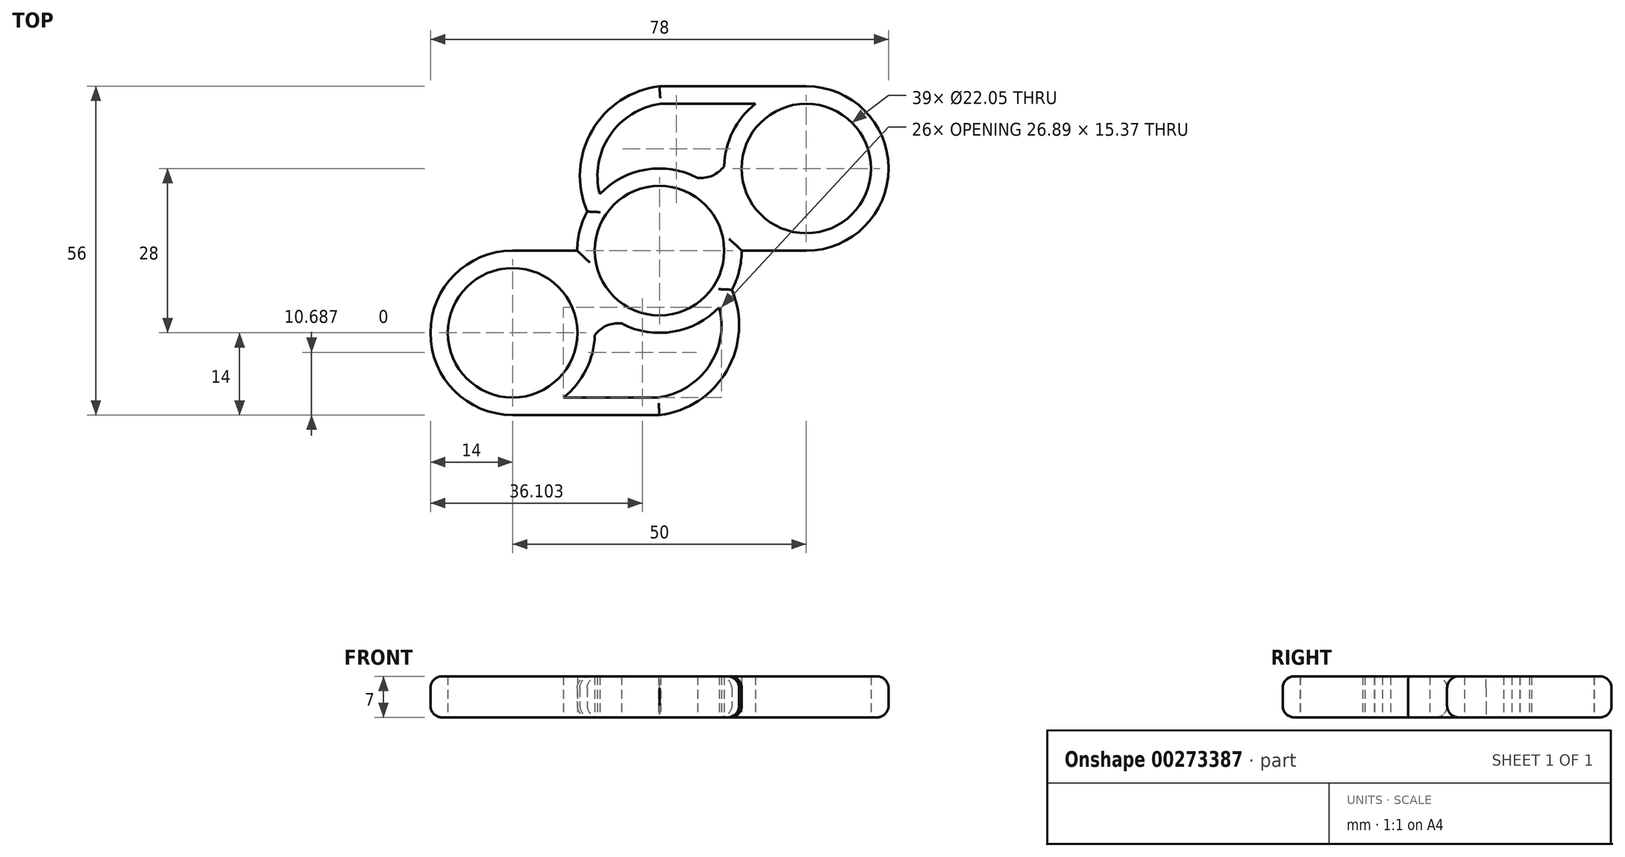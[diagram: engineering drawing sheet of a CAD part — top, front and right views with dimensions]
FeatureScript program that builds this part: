
annotation { "Feature Type Name" : "Feature", "Feature Type Description" : "" }
export const myFeature = defineFeature(function(context is Context, id is Id, definition is map)
    precondition{}
    {
        {
            var Q0;
            Q0=qCreatedBy(makeId("Top.planeOp"),FACE);
            var sketch = newSketch(context, id + "F0", { "sketchPlane" : qUnion([Q0])});
            skCircle(sketch, "E0", {"center": v(0, 0) * mm, "radius": 11.02 * mm});
            skCircle(sketch, "E1", {"center": v(25, 14) * mm, "radius": 11.03 * mm});
            skArc(sketch, "E2", {"start": v(16.34, 25) * mm, "mid": v(12.49, 20.28) * mm, "end": v(11, 14.38) * mm});
            skArc(sketch, "E3", {"start": v(6.48, 12.41) * mm, "mid": v(-2.31, 13.8) * mm, "end": v(-10.17, 9.63) * mm});
            skLineSegment(sketch, "E4", {"start": v(25, 28) * mm, "end": v(0, 28) * mm});
            skArc(sketch, "E5", {"start": v(0, 28) * mm, "mid": v(-11.5, 20.4) * mm, "end": v(-12.32, 6.66) * mm});
            skArc(sketch, "E6.0", {"start": v(0.19, 25) * mm, "mid": v(-8.44, 19.64) * mm, "end": v(-10.17, 9.63) * mm});
            skLineSegment(sketch, "E6.1", {"start": v(26.9, 25) * mm, "end": v(24.26, 25) * mm});
            skLineSegment(sketch, "E7", {"start": v(25, 0) * mm, "end": v(14, 0) * mm});
            skArc(sketch, "E8", {"start": v(6.48, 12.41) * mm, "mid": v(9, 12.78) * mm, "end": v(11, 14.38) * mm});
            skLineSegment(sketch, "E9.trimOffspring", {"start": v(16.34, 25) * mm, "end": v(0.19, 25) * mm});
            skArc(sketch, "E10.trimOffspring", {"start": v(25, 0) * mm, "mid": v(39, 14) * mm, "end": v(25, 28) * mm});
            skArc(sketch, "E11.trimOffspring", {"start": v(-12.32, 6.66) * mm, "mid": v(-13.57, 3.43) * mm, "end": v(-14, 0) * mm});
            skArc(sketch, "E12.1.0", {"start": v(-25, 0) * mm, "mid": v(-39, -14) * mm, "end": v(-25, -28) * mm});
            skLineSegment(sketch, "E12.1.1", {"start": v(-16.34, -25) * mm, "end": v(-0.19, -25) * mm});
            skLineSegment(sketch, "E12.1.2", {"start": v(-25, 0) * mm, "end": v(-14, 0) * mm});
            skLineSegment(sketch, "E12.1.3", {"start": v(-25, -28) * mm, "end": v(0, -28) * mm});
            skArc(sketch, "E12.1.4", {"start": v(-16.34, -25) * mm, "mid": v(-12.49, -20.28) * mm, "end": v(-11, -14.38) * mm});
            skCircle(sketch, "E12.1.5", {"center": v(-25, -14) * mm, "radius": 11.03 * mm});
            skLineSegment(sketch, "E12.1.6", {"start": v(-26.9, -25) * mm, "end": v(-24.26, -25) * mm});
            skArc(sketch, "E12.1.7", {"start": v(-6.48, -12.41) * mm, "mid": v(-9, -12.78) * mm, "end": v(-11, -14.38) * mm});
            skArc(sketch, "E12.1.8", {"start": v(-0.19, -25) * mm, "mid": v(8.44, -19.64) * mm, "end": v(10.17, -9.63) * mm});
            skArc(sketch, "E12.1.9", {"start": v(0, -28) * mm, "mid": v(11.5, -20.4) * mm, "end": v(12.32, -6.66) * mm});
            skArc(sketch, "E13.trimOffspring", {"start": v(-6.48, -12.41) * mm, "mid": v(2.31, -13.8) * mm, "end": v(10.17, -9.63) * mm});
            skArc(sketch, "E14.trimOffspring", {"start": v(12.32, -6.66) * mm, "mid": v(13.57, -3.43) * mm, "end": v(14, 0) * mm});
            skSolve(sketch);
        }
        {
            var Q0;
            Q0=makeQuery(id+"F0.imprint","IMPRINT",FACE,{"disambiguationData":[TD([[makeQuery(id+"F0.imprint","IMPRINT",EDGE,{"derivedFrom":sQuery(id+"F0.wireOp",EDGE,"E0")}),-1.0]])]});
            extrude(context, id + "F1", {"entities" : qUnion([Q0]), "depth" : 7 * mm});
        }
        {
            var Q0;
            Q0=makeQuery(id+"F1.opExtrude","CAP_EDGE",EDGE,{"disambiguationData":[OSD([sQuery(id+"F0.wireOp",EDGE,"E12.1.3")])],"isStart":false});
            var Q1;
            Q1=makeQuery(id+"F1.opExtrude","CAP_EDGE",EDGE,{"disambiguationData":[OSD([sQuery(id+"F0.wireOp",EDGE,"E12.1.0")])],"isStart":false});
            var Q2;
            Q2=makeQuery(id+"F1.opExtrude","CAP_EDGE",EDGE,{"disambiguationData":[OSD([sQuery(id+"F0.wireOp",EDGE,"E5")])],"isStart":false});
            var Q3;
            Q3=makeQuery(id+"F1.opExtrude","CAP_EDGE",EDGE,{"disambiguationData":[OSD([sQuery(id+"F0.wireOp",EDGE,"E11.trimOffspring")])],"isStart":false});
            var Q4;
            Q4=makeQuery(id+"F1.opExtrude","CAP_EDGE",EDGE,{"disambiguationData":[OSD([sQuery(id+"F0.wireOp",EDGE,"E12.1.2")])],"isStart":false});
            var Q5;
            Q5=makeQuery(id+"F1.opExtrude","CAP_EDGE",EDGE,{"disambiguationData":[OSD([sQuery(id+"F0.wireOp",EDGE,"E12.1.9")])],"isStart":false});
            var Q6;
            Q6=makeQuery(id+"F1.opExtrude","CAP_EDGE",EDGE,{"disambiguationData":[OSD([sQuery(id+"F0.wireOp",EDGE,"E14.trimOffspring")])],"isStart":false});
            var Q7;
            Q7=makeQuery(id+"F1.opExtrude","CAP_EDGE",EDGE,{"disambiguationData":[OSD([sQuery(id+"F0.wireOp",EDGE,"E7")])],"isStart":false});
            var Q8;
            Q8=makeQuery(id+"F1.opExtrude","CAP_EDGE",EDGE,{"disambiguationData":[OSD([sQuery(id+"F0.wireOp",EDGE,"E10.trimOffspring")])],"isStart":false});
            var Q9;
            Q9=makeQuery(id+"F1.opExtrude","CAP_EDGE",EDGE,{"disambiguationData":[OSD([sQuery(id+"F0.wireOp",EDGE,"E4")])],"isStart":false});
            var Q10;
            Q10=makeQuery(id+"F1.opExtrude","CAP_EDGE",EDGE,{"disambiguationData":[OSD([sQuery(id+"F0.wireOp",EDGE,"E12.1.2")])],"isStart":true});
            var Q11;
            Q11=makeQuery(id+"F1.opExtrude","CAP_EDGE",EDGE,{"disambiguationData":[OSD([sQuery(id+"F0.wireOp",EDGE,"E12.1.9")])],"isStart":true});
            var Q12;
            Q12=makeQuery(id+"F1.opExtrude","CAP_EDGE",EDGE,{"disambiguationData":[OSD([sQuery(id+"F0.wireOp",EDGE,"E14.trimOffspring")])],"isStart":true});
            var Q13;
            Q13=makeQuery(id+"F1.opExtrude","CAP_EDGE",EDGE,{"disambiguationData":[OSD([sQuery(id+"F0.wireOp",EDGE,"E7")])],"isStart":true});
            var Q14;
            Q14=makeQuery(id+"F1.opExtrude","CAP_EDGE",EDGE,{"disambiguationData":[OSD([sQuery(id+"F0.wireOp",EDGE,"E10.trimOffspring")])],"isStart":true});
            var Q15;
            Q15=makeQuery(id+"F1.opExtrude","CAP_EDGE",EDGE,{"disambiguationData":[OSD([sQuery(id+"F0.wireOp",EDGE,"E5")])],"isStart":true});
            var Q16;
            Q16=makeQuery(id+"F1.opExtrude","CAP_EDGE",EDGE,{"disambiguationData":[OSD([sQuery(id+"F0.wireOp",EDGE,"E11.trimOffspring")])],"isStart":true});
            fillet(context, id + "F2", {"entities" : qUnion([Q0, Q1, Q2, Q3, Q4, Q5, Q6, Q7, Q8, Q9, Q10, Q11, Q12, Q13, Q14, Q15, Q16]), "radius" : 2 * mm, "tangentPropagation" : true, "allowEdgeOverflow" : false});
        }
    });
